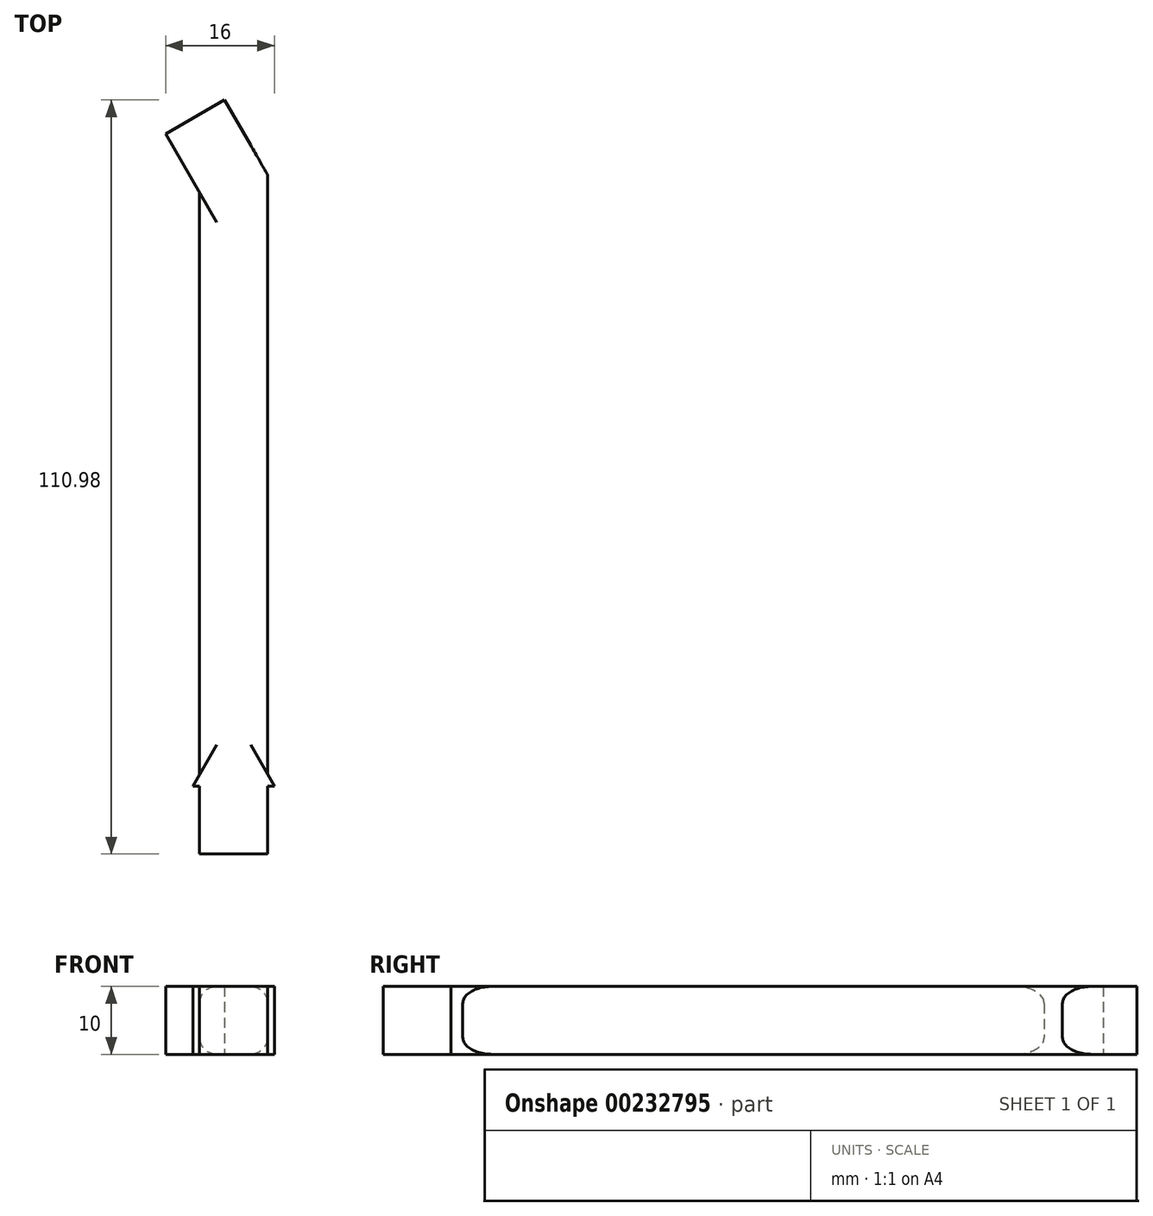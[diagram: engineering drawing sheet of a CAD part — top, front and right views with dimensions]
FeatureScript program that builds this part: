
annotation { "Feature Type Name" : "Feature", "Feature Type Description" : "" }
export const myFeature = defineFeature(function(context is Context, id is Id, definition is map)
    precondition{}
    {
        {
            var Q0;
            Q0=qCreatedBy(makeId("Top.planeOp"),FACE);
            var sketch = newSketch(context, id + "F0", { "sketchPlane" : qUnion([Q0])});
            skLineSegment(sketch, "E0.top", {"start": v(0, -71.64) * mm, "end": v(10, -71.64) * mm});
            skLineSegment(sketch, "E0.left", {"start": v(0, 25.68) * mm, "end": v(0, -59.9) * mm});
            skLineSegment(sketch, "E0.right", {"start": v(10, 28.36) * mm, "end": v(10, -59.9) * mm});
            skLineSegment(sketch, "E1.bottom", {"start": v(-5, 34.34) * mm, "end": v(0, 25.68) * mm});
            skLineSegment(sketch, "E1.top", {"start": v(3.66, 39.34) * mm, "end": v(10, 28.36) * mm});
            skLineSegment(sketch, "E1.right", {"start": v(-5, 34.34) * mm, "end": v(3.66, 39.34) * mm});
            skPoint(sketch, "E2", {"position": v(0, 25.68) * mm});
            skLineSegment(sketch, "E3", {"start": v(3.66, 39.34) * mm, "end": v(-30.84, 19.42) * mm, "construction": true});
            skLineSegment(sketch, "E4", {"start": v(-1, -61.64) * mm, "end": v(0, -61.64) * mm});
            skLineSegment(sketch, "E5.trimOffspring", {"start": v(10, -61.64) * mm, "end": v(11, -61.64) * mm});
            skLineSegment(sketch, "E6", {"start": v(-1, -61.64) * mm, "end": v(0, -59.9) * mm});
            skLineSegment(sketch, "E7", {"start": v(10, -59.9) * mm, "end": v(11, -61.64) * mm});
            skLineSegment(sketch, "E8.trimOffspring", {"start": v(0, -61.64) * mm, "end": v(0, -71.64) * mm});
            skLineSegment(sketch, "E9.trimOffspring", {"start": v(10, -61.64) * mm, "end": v(10, -71.64) * mm});
            skSolve(sketch);
        }
        {
            var Q0;
            Q0=makeQuery(id+"F0.imprint","IMPRINT",FACE,{"disambiguationData":[TD([[makeQuery(id+"F0.imprint","IMPRINT",EDGE,{"derivedFrom":sQuery(id+"F0.wireOp",EDGE,"E0.top")}),1.0]])]});
            extrude(context, id + "F1", {"entities" : qUnion([Q0]), "depth" : 10 * mm});
        }
        {
            var Q0;
            Q0=makeQuery(id+"F1.opExtrude","CAP_EDGE",EDGE,{"disambiguationData":[OSD([sQuery(id+"F0.wireOp",EDGE,"E0.left")])],"isStart":false});
            var Q1;
            Q1=makeQuery(id+"F1.opExtrude","CAP_EDGE",EDGE,{"disambiguationData":[OSD([sQuery(id+"F0.wireOp",EDGE,"E0.left")])],"isStart":true});
            var Q2;
            Q2=makeQuery(id+"F1.opExtrude","CAP_EDGE",EDGE,{"disambiguationData":[OSD([sQuery(id+"F0.wireOp",EDGE,"E0.right")])],"isStart":false});
            var Q3;
            Q3=makeQuery(id+"F1.opExtrude","CAP_EDGE",EDGE,{"disambiguationData":[OSD([sQuery(id+"F0.wireOp",EDGE,"E0.right")])],"isStart":true});
            fillet(context, id + "F2", {"entities" : qUnion([Q0, Q1, Q2, Q3]), "radius" : 2.5 * mm, "allowEdgeOverflow" : false});
        }
    });
